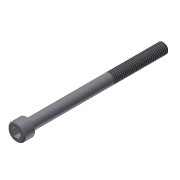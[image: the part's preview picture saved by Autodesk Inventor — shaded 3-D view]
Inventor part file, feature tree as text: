
AUTODESK INVENTOR PART (.ipt)
format: ipt  version: 2011 (Build 150239000, 239)  size: 94,720 bytes
history: native  units: in
note: dims shown in document units (in); Inventor stores cm internally (conversion verified against a paired STEP export)
features: extrude x3, sketch x3, chamfer x2, thread x1
ambient origin geometry x8: Origin, YZ Plane, XZ Plane, XY Plane, X Axis, Y Axis, Z Axis, Center Point
bodies: Solid1 (feature_tree)
feature tree (9):
  extrude  "Extrusion1"  Depth=0.19in TaperAngle=0.0deg
  extrude  "Extrusion2"  Depth=2.5in TaperAngle=0.0deg
  extrude  "Extrusion3"  Depth=0.125in TaperAngle=0.0deg
  thread  "Thread1"  [1 undecoded]
  chamfer  "Chamfer1"  Distance=0.02in Angle=45.0deg
  chamfer  "Chamfer2"  Distance=0.02in Angle=45.0deg
  sketch  "Sketch1"  dims[d0=0.312in d1=0.19in d2=0.0in]
  sketch  "Sketch2"  dims[d3=0.19in d4=2.5in d5=0.0in]
  sketch  "Sketch3"  dims[d6=0.1562in d7=0.125in d8=0.0in d9=1.0in d10=0.0in d11=0.02in d12=0.125in d13=45.0deg d14=0.02in d15=0.125in d16=45.0deg]
note: 1 required parameter value undecoded (feature->parameter linkage not recoverable at this tier; creation-order binding heuristic only, values carry confidence <= 0.55)
